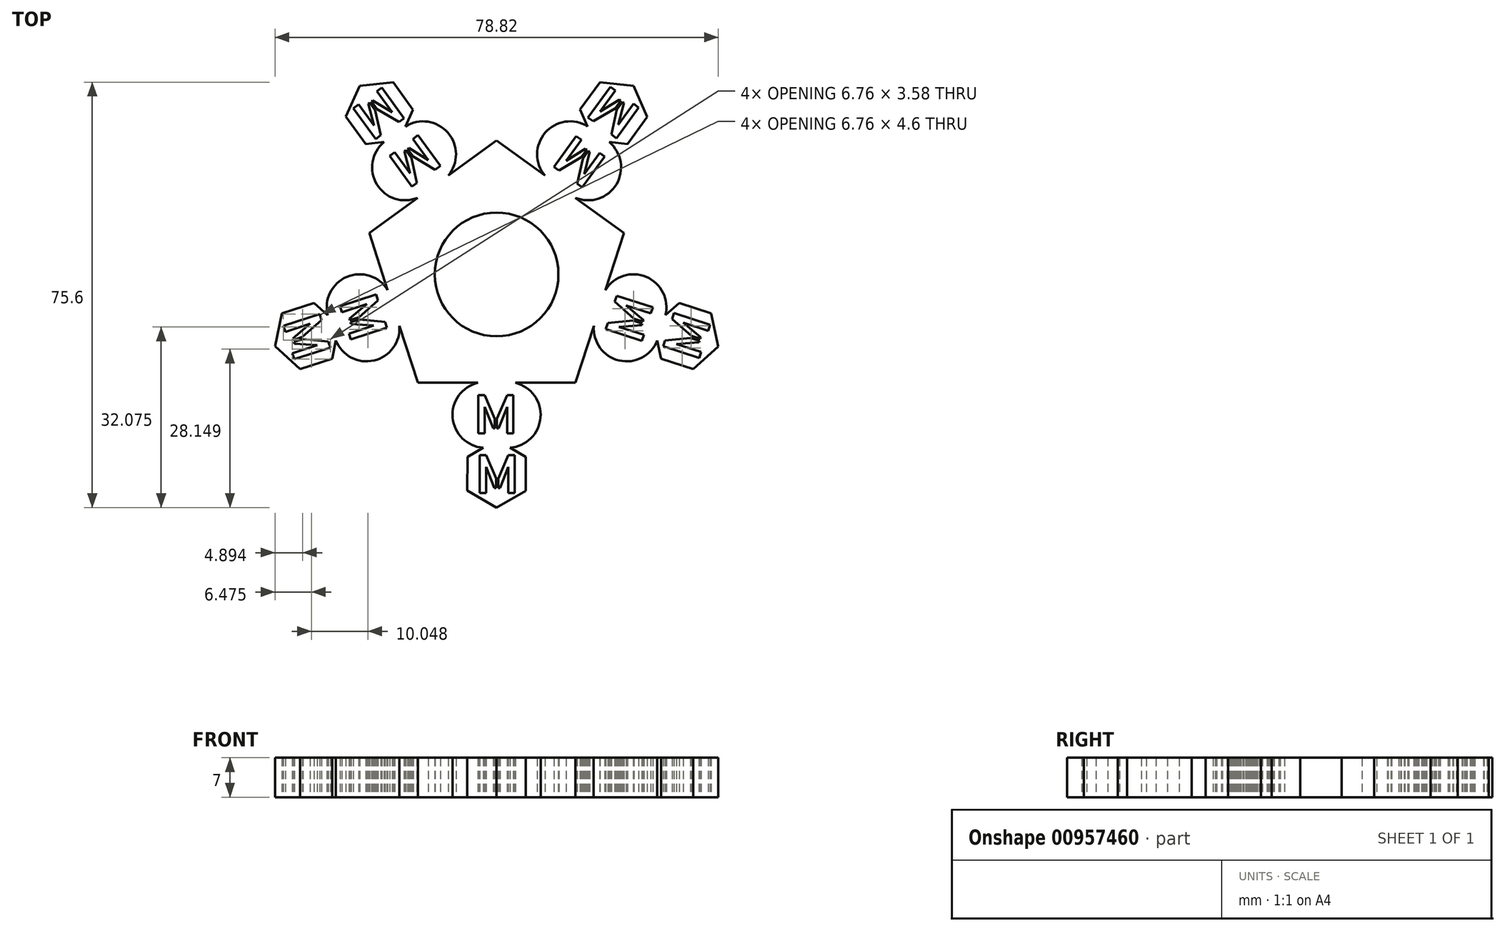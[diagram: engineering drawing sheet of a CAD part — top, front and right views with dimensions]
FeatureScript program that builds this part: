
annotation { "Feature Type Name" : "Feature", "Feature Type Description" : "" }
export const myFeature = defineFeature(function(context is Context, id is Id, definition is map)
    precondition{}
    {
        {
            var Q0;
            Q0=qCreatedBy(makeId("Top.planeOp"),FACE);
            var sketch = newSketch(context, id + "F0", { "sketchPlane" : qUnion([Q0])});
            skLineSegment(sketch, "E0", {"start": v(0, 0) * mm, "end": v(255.48, 0) * mm, "construction": true});
            skCircle(sketch, "E1", {"center": v(0, 0) * mm, "radius": 40 * mm, "construction": true});
            skCircle(sketch, "E2", {"center": v(0, 0) * mm, "radius": 11 * mm});
            skCircle(sketch, "E3.cCircle", {"center": v(0, 0) * mm, "radius": 19.27 * mm, "construction": true});
            skLineSegment(sketch, "E3.0", {"start": v(14, -19.27) * mm, "end": v(-14, -19.27) * mm});
            skLineSegment(sketch, "E3.1", {"start": v(-14, -19.27) * mm, "end": v(-22.65, 7.36) * mm});
            skLineSegment(sketch, "E3.2", {"start": v(-22.65, 7.36) * mm, "end": v(0, 23.82) * mm});
            skLineSegment(sketch, "E3.3", {"start": v(0, 23.82) * mm, "end": v(22.65, 7.36) * mm});
            skLineSegment(sketch, "E3.4", {"start": v(22.65, 7.36) * mm, "end": v(14, -19.27) * mm});
            skPoint(sketch, "E3.0.midPoint", {"position": v(0, -19.27) * mm});
            skArc(sketch, "E4", {"start": v(-3.35, -19.27) * mm, "mid": v(-7.81, -25.46) * mm, "end": v(-2.37, -30.8) * mm});
            skLineSegment(sketch, "E5", {"start": v(0, -0.68) * mm, "end": v(0, -58.26) * mm, "construction": true});
            skArc(sketch, "E6.MirrorCS", {"start": v(3.35, -19.27) * mm, "mid": v(7.81, -25.46) * mm, "end": v(2.37, -30.8) * mm});
            skCircle(sketch, "E7", {"center": v(0, -35.44) * mm, "radius": 6 * mm, "construction": true});
            skLineSegment(sketch, "E8.0", {"start": v(5.2, -32.45) * mm, "end": v(5.19, -38.45) * mm});
            skLineSegment(sketch, "E8.1", {"start": v(5.19, -38.45) * mm, "end": v(-0.01, -41.44) * mm});
            skLineSegment(sketch, "E8.2", {"start": v(-0.01, -41.44) * mm, "end": v(-5.2, -38.43) * mm});
            skLineSegment(sketch, "E8.3", {"start": v(-5.2, -38.43) * mm, "end": v(-5.19, -32.43) * mm});
            skLineSegment(sketch, "E8.4", {"start": v(-5.19, -32.43) * mm, "end": v(0.01, -29.44) * mm});
            skLineSegment(sketch, "E8.5", {"start": v(0.01, -29.44) * mm, "end": v(5.2, -32.45) * mm});
            skPoint(sketch, "E9.orphan", {"position": v(-3.55, -30.6) * mm});
            skPoint(sketch, "E10.orphan", {"position": v(3.55, -30.6) * mm});
            skText(sketch, "E11", { "text": "M", "fontName": "AllertaStencil-Regular.ttf"});
            skText(sketch, "E12", { "text": "M", "fontName": "AllertaStencil-Regular.ttf"});
            const initialGuessF0  = {"E11": [-0.00408, -0.02823, 1, 0, 0.00675], "E12": [-0.00385, -0.03887, 1, 0, 0.00675]};
            skSetInitialGuess(sketch, initialGuessF0);
            skSolve(sketch);
        }
        {
            var Q0;
            Q0 = qSketchRegion(id + "F0", true);
            extrude(context, id + "F1", {"entities" : qUnion([Q0]), "depth" : 7 * mm, "offsetDistance" : 25 * mm});
        }
        {
            var Q0;
            Q0=makeQuery(id+"F1.opExtrude","SWEPT_BODY",BODY,{"disambiguationData":[OSD([sQuery(id+"F0.wireOp",EDGE,"E2"),sQuery(id+"F0.wireOp",EDGE,"E3.0"),sQuery(id+"F0.wireOp",EDGE,"E3.1"),sQuery(id+"F0.wireOp",EDGE,"E3.2"),sQuery(id+"F0.wireOp",EDGE,"E3.3"),sQuery(id+"F0.wireOp",EDGE,"E3.4"),sQuery(id+"F0.wireOp",EDGE,"E4"),sQuery(id+"F0.wireOp",EDGE,"E6.MirrorCS"),sQuery(id+"F0.wireOp",EDGE,"E8.0"),sQuery(id+"F0.wireOp",EDGE,"E8.1"),sQuery(id+"F0.wireOp",EDGE,"E8.2"),sQuery(id+"F0.wireOp",EDGE,"E8.3"),sQuery(id+"F0.wireOp",EDGE,"E8.4"),sQuery(id+"F0.wireOp",EDGE,"E8.5")])]});
            var Q1;
            Q1=makeQuery(id+"F1.opExtrude","CAP_EDGE",EDGE,{"disambiguationData":[OSD([sQuery(id+"F0.wireOp",EDGE,"E2")])],"isStart":false});
            circularPattern(context, id + "F2", {"operationType" : NewBodyOperationType.ADD, "entities" : qUnion([Q0]), "axis" : qUnion([Q1]), "angle" : 360 * degree, "instanceCount" : 5, "equalSpace" : true});
        }
    });
